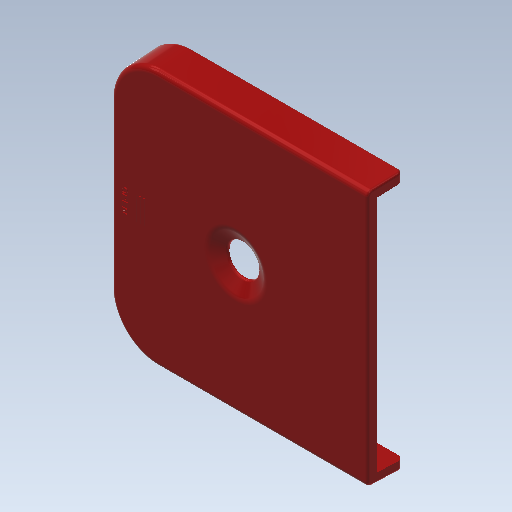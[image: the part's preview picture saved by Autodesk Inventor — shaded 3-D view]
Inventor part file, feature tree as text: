
AUTODESK INVENTOR PART (.ipt)
format: ipt  version: 2020 (Build 240168000, 168)  size: 391,168 bytes
history: native  units: in
note: dims shown in document units (in); Inventor stores cm internally (conversion verified against a paired STEP export)
features: fillet x7, plane x5, sketch x4, extrude x2, reference x2, draft x1, shell x1, mirror x1, hole x1, emboss x1
ambient origin geometry x8: Origin, YZ Plane, XZ Plane, XY Plane, X Axis, Y Axis, Z Axis, Center Point
bodies: Body1 (feature_tree)
feature tree (25):
  plane  "Work Plane1"
  plane  "Work Plane2"
  sketch  "Sketch2"  dims[d7=0.252in d8=0.0in d12=0.0137in d13=0.354in d14=0.071in]
  plane  "Work Plane3"
  extrude  "Extrusion3"  Depth=0.0137in
  plane  "Work Plane4"
  draft  "FaceDraft3"
  fillet  "Fillet5"  Radius=0.354in
  shell  "Shell1"  Thickness=0.071in
  extrude  "Extrusion4"  Depth=0.217in
  fillet  "Fillet6"  Radius=0.071in
  plane  "Work Plane5"
  mirror  "Mirror1"
  hole  "Hole1"  [1 undecoded]
  fillet  "Fillet7"  Radius=0.236in
  fillet  "Fillet8"  Radius=0.02in
  fillet  "Fillet9"  Radius=0.079in
  fillet  "Fillet10"  Radius=0.039in
  fillet  "Fillet11"  Radius=0.039in
  emboss  "Emboss1"
  reference  "Reference3"
  sketch  "Sketch4"  dims[d15=0.01in d16=0.217in d17=0.071in]
  sketch  "Sketch6"  dims[d18=0.252in d19=0.0in d20=0.02in d24=0.236in]
  reference  "Reference4"
  sketch  "Sketch7"  dims[d30=0.236in d31=0.75in d32=0.433in d33=0.25in d34=120.0deg d35=0.125in d36=0.8108in d37=0.02in d38=0.079in d39=0.039in d40=0.039in d41=0.02in d43=0.008in d44=0.0in]
note: 1 required parameter value undecoded (feature->parameter linkage not recoverable at this tier; creation-order binding heuristic only, values carry confidence <= 0.55)
